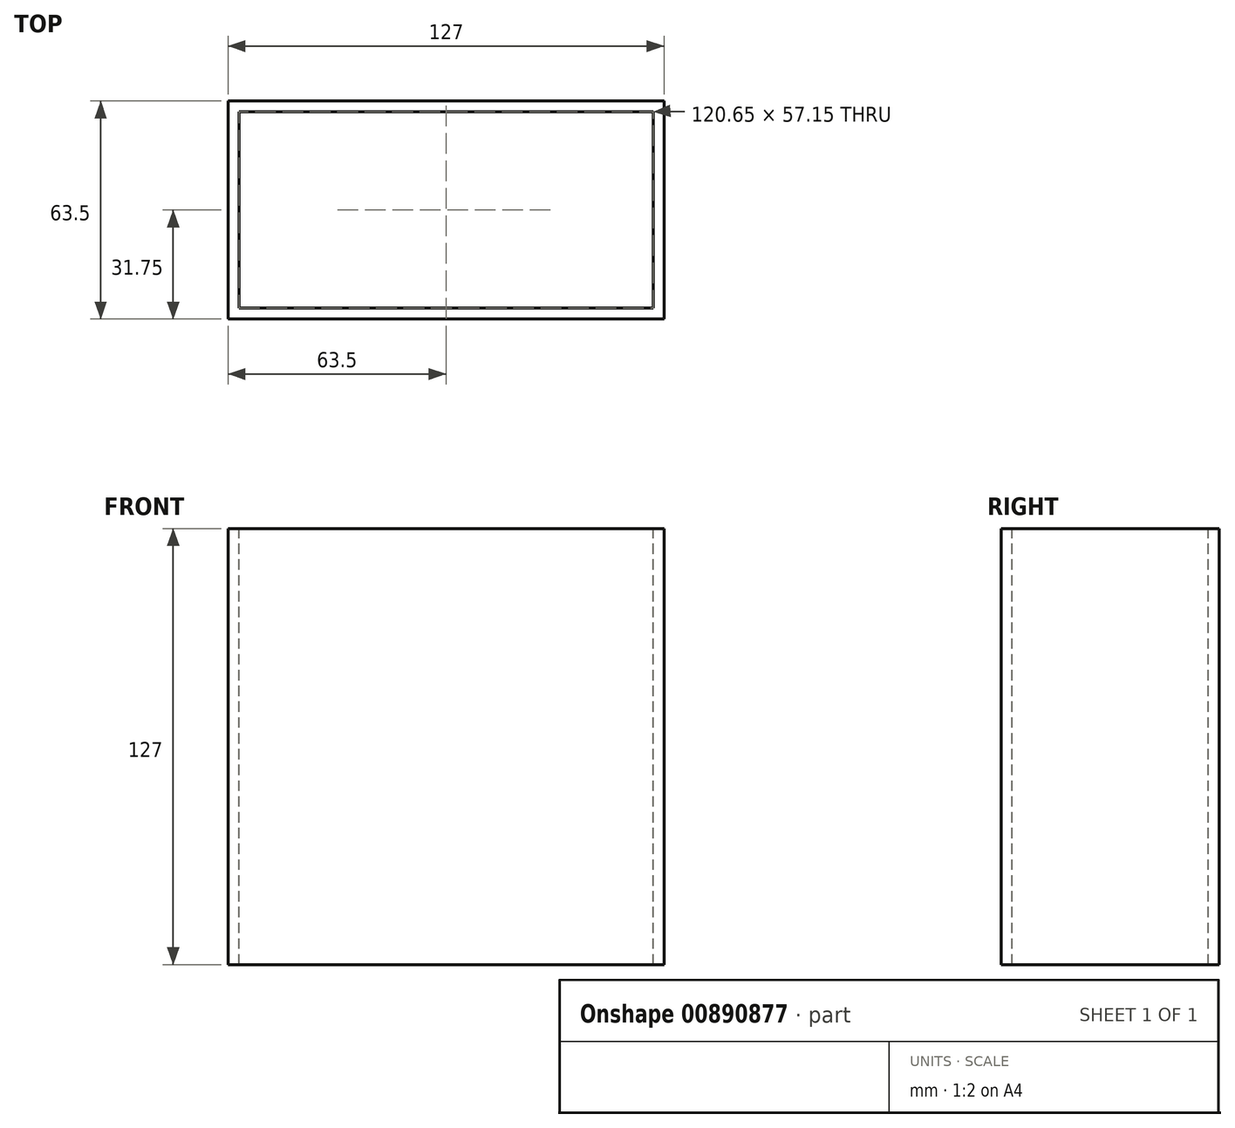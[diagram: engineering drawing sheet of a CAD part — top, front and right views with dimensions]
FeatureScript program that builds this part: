
annotation { "Feature Type Name" : "Feature", "Feature Type Description" : "" }
export const myFeature = defineFeature(function(context is Context, id is Id, definition is map)
    precondition{}
    {
        {
            var Q0;
            Q0=qCreatedBy(makeId("Top.planeOp"),FACE);
            var sketch = newSketch(context, id + "F0", { "sketchPlane" : qUnion([Q0])});
            skLineSegment(sketch, "E0.bottom", {"start": v(0, 0) * mm, "end": v(127, 0) * mm});
            skLineSegment(sketch, "E0.top", {"start": v(0, 63.5) * mm, "end": v(127, 63.5) * mm});
            skLineSegment(sketch, "E0.left", {"start": v(0, 0) * mm, "end": v(0, 63.5) * mm});
            skLineSegment(sketch, "E0.right", {"start": v(127, 0) * mm, "end": v(127, 63.5) * mm});
            skSolve(sketch);
        }
        {
            var Q0;
            Q0=makeQuery(id+"F0.imprint","IMPRINT",FACE,{"disambiguationData":[TD([[makeQuery(id+"F0.imprint","IMPRINT",EDGE,{"derivedFrom":sQuery(id+"F0.wireOp",EDGE,"E0.bottom")}),1.0]])]});
            extrude(context, id + "F1", {"entities" : qUnion([Q0]), "depth" : 127 * mm, "offsetDistance" : 25.4 * mm});
        }
        {
            var Q0;
            Q0=makeQuery(id+"F1.opExtrude","CAP_FACE",FACE,{"disambiguationData":[OSD([sQuery(id+"F0.wireOp",EDGE,"E0.bottom"),sQuery(id+"F0.wireOp",EDGE,"E0.top"),sQuery(id+"F0.wireOp",EDGE,"E0.left"),sQuery(id+"F0.wireOp",EDGE,"E0.right")])],"isStart":false});
            var sketch = newSketch(context, id + "F2", { "sketchPlane" : qUnion([Q0])});
            skLineSegment(sketch, "E1.bottom", {"start": v(123.82, 60.33) * mm, "end": v(3.17, 60.33) * mm});
            skLineSegment(sketch, "E1.top", {"start": v(123.83, 3.18) * mm, "end": v(3.17, 3.17) * mm});
            skLineSegment(sketch, "E1.left", {"start": v(123.83, 60.33) * mm, "end": v(123.83, 3.17) * mm});
            skLineSegment(sketch, "E1.right", {"start": v(3.17, 60.33) * mm, "end": v(3.17, 3.17) * mm});
            skPoint(sketch, "E1.middle", {"position": v(63.5, 31.75) * mm});
            skPoint(sketch, "E1.middle.positionSnap0", {"position": v(0, 31.75) * mm});
            skPoint(sketch, "E1.middle.positionSnap1", {"position": v(63.5, 63.5) * mm});
            skPoint(sketch, "E1.centerSnap0", {"position": v(0, 31.75) * mm});
            skPoint(sketch, "E1.centerSnap1", {"position": v(63.5, 63.5) * mm});
            skSolve(sketch);
        }
        {
            var Q0;
            Q0=makeQuery(id+"F2.imprint","IMPRINT",FACE,{"disambiguationData":[TD([[makeQuery(id+"F2.imprint","IMPRINT",EDGE,{"derivedFrom":sQuery(id+"F2.wireOp",EDGE,"E1.bottom")}),1.0]])]});
            extrude(context, id + "F3", {"entities" : qUnion([Q0]), "operationType" : NewBodyOperationType.REMOVE, "endBound" : BoundingType.THROUGH_ALL, "oppositeDirection" : true, "depth" : 25.4 * mm, "offsetDistance" : 25.4 * mm});
        }
    });
